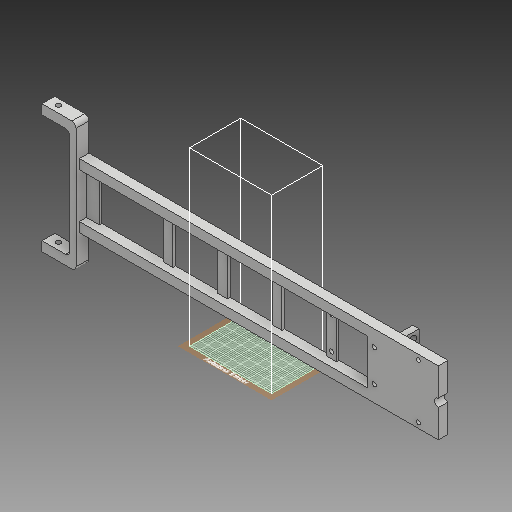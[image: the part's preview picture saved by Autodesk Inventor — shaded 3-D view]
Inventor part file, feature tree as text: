
AUTODESK INVENTOR PART (.ipt)
format: ipt  version: 2018 (Build 220112000, 112)  size: 913,408 bytes
history: native  units: mm
features: sketch x64, extrude x49, fillet x13, hole x6, plane x1
ambient origin geometry x8: Origin, YZ Plane, XZ Plane, XY Plane, X Axis, Y Axis, Z Axis, Center Point
bodies: Solid1 (feature_tree)
feature tree (133):
  extrude  "Extrusion1"  Depth=50.0mm
  hole  "Hole1"  [1 undecoded]
  hole  "Hole2"  [1 undecoded]
  extrude  "Extrusion2"  Depth=25.0mm
  extrude  "Extrusion3"  Depth=25.0mm
  extrude  "Extrusion4"  Depth=5.0mm
  sketch  "Sketch7"  dims[d25=10.0mm d26=5.0mm]
  extrude  "Extrusion5"  Depth=5.0mm
  extrude  "Extrusion6"  Depth=35.0mm
  extrude  "Extrusion7"  Depth=35.0mm
  extrude  "Extrusion8"  Depth=35.0mm
  extrude  "Extrusion9"  Depth=2.0mm TaperAngle=0.0deg
  extrude  "Extrusion10"  Depth=7.5mm TaperAngle=0.0deg
  extrude  "Extrusion11"  Depth=10.0mm
  extrude  "Extrusion12"  Depth=7.5mm
  fillet  "Fillet1"  Radius=7.5mm
  fillet  "Fillet2"  Radius=25.0mm
  fillet  "Fillet3"  Radius=3.0mm
  fillet  "Fillet4"  Radius=3.2mm
  fillet  "Fillet5"  Radius=2.1mm
  fillet  "Fillet6"  Radius=5.5mm
  extrude  "Extrusion13"  Depth=92.5mm TaperAngle=0.0deg
  sketch  "Sketch17"  dims[d58=4.25mm d59=241.0mm d60=0.0mm]
  hole  "Hole3"  [1 undecoded]
  hole  "Hole4"  [1 undecoded]
  extrude  "Extrusion14"  Depth=5.0mm
  extrude  "Extrusion15"  Depth=2.5mm TaperAngle=0.0deg
  extrude  "Extrusion16"  Depth=6.35mm
  extrude  "Extrusion17"  Depth=2.5mm
  extrude  "Extrusion18"  Depth=14.55mm TaperAngle=0.0deg
  extrude  "Extrusion19"  Depth=0.1mm
  extrude  "Extrusion20"  Depth=3.25mm
  extrude  "Extrusion21"  Depth=3.25mm
  hole  "Hole5"  [1 undecoded]
  extrude  "Extrusion22"  Depth=2.0mm
  extrude  "Extrusion23"  Depth=15.0mm
  extrude  "Extrusion24"  Depth=10.0mm TaperAngle=0.0deg
  hole  "Hole6"  [1 undecoded]
  extrude  "Extrusion25"  Depth=100.0mm TaperAngle=0.0deg
  extrude  "Extrusion26"  Depth=2.0mm TaperAngle=0.0deg
  sketch  "Sketch35"  dims[d116=3.3mm d117=3.3mm]
  plane  "Work Plane1"
  sketch  "Sketch36"  dims[d118=3.3mm d119=3.3mm d120=2.0mm d121=0.0mm]
  extrude  "Extrusion27"  Depth=3.3mm
  extrude  "Extrusion28"  Depth=2.0mm
  fillet  "Fillet7"  Radius=2.0mm
  extrude  "Extrusion29"  Depth=8.0mm
  extrude  "Extrusion30"  Depth=21.0mm
  extrude  "Extrusion31"  Depth=8.5mm
  extrude  "Extrusion32"  Depth=3.5mm
  sketch  "Sketch43"  dims[d142=10.0mm d143=0.0mm d144=7.5mm d145=0.0mm]
  fillet  "Fillet8"  Radius=3.3mm
  extrude  "Extrusion33"  Depth=3.3mm
  extrude  "Extrusion34"  Depth=7.5mm TaperAngle=0.0deg
  extrude  "Extrusion35"  Depth=15.0mm
  extrude  "Extrusion36"  Depth=100.0mm TaperAngle=0.0deg
  extrude  "Extrusion37"  Depth=5.0mm
  fillet  "Fillet9"  Radius=5.0mm
  fillet  "Fillet10"  Radius=37.5mm
  fillet  "Fillet11"  Radius=1.1mm
  fillet  "Fillet12"  Radius=37.5mm
  sketch  "Sketch49"  dims[d170=5.5mm d171=0.0mm d172=10.0mm d173=0.0mm]
  extrude  "Extrusion38"  Depth=3.0mm
  extrude  "Extrusion39"  Depth=10.0mm TaperAngle=0.0deg
  extrude  "Extrusion40"  Depth=74.724mm
  fillet  "Fillet13"  Radius=85.515mm
  extrude  "Extrusion41"  Depth=5.0mm
  extrude  "Extrusion42"  Depth=5.0mm
  sketch  "Sketch55"  dims[d186=10.0mm d187=2.0mm d188=0.0mm]
  extrude  "Extrusion43"  Depth=5.0mm
  extrude  "Extrusion44"  Depth=2.0mm TaperAngle=0.0deg
  sketch  "Sketch58"  dims[d195=1.0mm d196=0.0mm d197=20.0mm]
  extrude  "Extrusion45"  Depth=2.0mm TaperAngle=0.0deg
  extrude  "Extrusion46"  Depth=1.0mm TaperAngle=0.0deg
  sketch  "Sketch61"  dims[d202=2.5mm d203=0.0mm]
  extrude  "Extrusion47"  Depth=10.0mm
  extrude  "Extrusion48"  Depth=20.0mm
  extrude  "Extrusion49"  Depth=7.5mm
  sketch  "Sketch1"  dims[d0=50.0mm d1=50.0mm]
  sketch  "Sketch2"  dims[d2=240.0mm d3=7.5mm]
  sketch  "Sketch3"  dims[d4=7.5mm d5=7.5mm d6=0.0mm]
  sketch  "Sketch4"  dims[d7=6.35mm d8=6.0mm d9=4.0mm d10=2.0mm d11=90.0deg d12=8.0mm d13=20.594885mm d14=25.0mm]
  sketch  "Sketch5"  dims[d15=3.3mm d16=6.0mm d17=4.0mm d18=2.0mm d19=90.0deg d20=8.0mm d21=20.594885mm d22=25.0mm]
  sketch  "Sketch6"  dims[d23=180.0deg d24=5.0mm]
  sketch  "Sketch8"  dims[d27=17.5mm d28=0.0mm d30=35.0mm]
  sketch  "Sketch9"  dims[d31=35.0mm d32=35.0mm]
  sketch  "Sketch10"  dims[d33=35.0mm d34=35.0mm]
  sketch  "Sketch11"  dims[d35=35.0mm d36=2.0mm d37=0.0mm]
  sketch  "Sketch12"  dims[d38=10.0mm d39=7.5mm d40=0.0mm]
  sketch  "Sketch13"  dims[d41=100.0mm d42=10.0mm]
  sketch  "Sketch14"  dims[d43=7.5mm d44=0.0mm d45=7.5mm d46=7.5mm d47=25.0mm d48=0.0mm d49=3.0mm d50=3.2mm d51=2.1mm d52=5.5mm]
  sketch  "Sketch15"  dims[d53=3.3mm d54=92.5mm d55=0.0mm]
  sketch  "Sketch16"  dims[d56=5.5mm d57=3.3mm]
  sketch  "Sketch18"  dims[d61=4.44mm d62=5.0mm]
  sketch  "Sketch19"  dims[d63=2.5mm d64=91.25mm d65=0.0mm]
  sketch  "Sketch20"  dims[d66=30.0mm d67=6.35mm]
  sketch  "Sketch21"  dims[d68=3.8mm d69=0.0mm d70=2.5mm]
  sketch  "Sketch22"  dims[d71=14.55mm d72=0.0mm d73=14.55mm d74=0.0mm]
  sketch  "Sketch23"  dims[d75=0.1mm d76=0.1mm]
  sketch  "Sketch24"  dims[d77=3.25mm d78=3.25mm]
  sketch  "Sketch25"  dims[d79=3.25mm d80=3.25mm]
  sketch  "Sketch26"  dims[d81=35.0mm d82=10.0mm]
  sketch  "Sketch27"  dims[d83=2.0mm d84=0.0mm d85=3.6mm]
  sketch  "Sketch28"  dims[d86=3.6mm]
  sketch  "Sketch29"  dims[d87=3.3mm d88=6.0mm d89=4.0mm d90=2.0mm d91=90.0deg d92=15.0mm d93=20.594885mm]
  sketch  "Sketch30"  dims[d94=3.3mm d95=6.0mm d96=4.0mm d97=2.0mm d98=90.0deg d99=15.0mm d100=20.594885mm d101=6.0mm]
  sketch  "Sketch31"  dims[d102=20.0mm d103=0.0mm d104=10.0mm d105=0.0mm]
  sketch  "Sketch32"  dims[d106=2.0mm d107=0.0mm d108=4.0mm]
  sketch  "Sketch33"  dims[d109=100.0mm d110=0.0mm d111=100.0mm d112=0.0mm]
  sketch  "Sketch34"  dims[d113=5.0mm d114=2.0mm d115=0.0mm]
  sketch  "Sketch37"  dims[d122=5.5mm d123=0.0mm]
  sketch  "Sketch38"  dims[d124=3.3mm d125=6.0mm d126=4.0mm d127=2.0mm d128=90.0deg d129=8.0mm d130=20.594885mm d131=42.0mm]
  sketch  "Sketch39"  dims[d132=17.0mm d133=21.0mm]
  sketch  "Sketch40"  dims[d135=8.5mm d136=15.825mm]
  sketch  "Sketch41"  dims[d137=3.5mm d138=21.0mm d139=3.3mm]
  sketch  "Sketch42"  dims[d140=3.3mm d141=3.3mm]
  sketch  "Sketch44"  dims[d146=100.0mm d147=0.0mm]
  sketch  "Sketch45"  dims[d148=5.0mm d149=6.0mm d150=4.0mm d151=2.0mm d152=90.0deg d153=15.0mm d154=0.0mm d155=3.75mm]
  sketch  "Sketch46"  dims[d156=100.0mm d157=0.0mm d158=100.0mm d159=0.0mm]
  sketch  "Sketch47"  dims[d160=-0.698132mm d161=5.0mm d162=5.0mm d163=37.5mm d164=0.0mm d165=1.1mm d166=37.5mm d167=0.0mm]
  sketch  "Sketch48"  dims[d168=0.2mm d169=3.0mm]
  sketch  "Sketch50"  dims[d174=74.724mm d175=74.724mm d176=85.515mm]
  sketch  "Sketch51"  dims[d177=5.0mm d178=85.515mm]
  sketch  "Sketch52"  dims[d179=5.0mm d180=85.515mm]
  sketch  "Sketch53"  dims[d181=5.0mm d182=85.515mm]
  sketch  "Sketch54"  dims[d183=5.0mm d184=2.0mm d185=0.0mm]
  sketch  "Sketch56"  dims[d189=2.0mm d190=1.0mm d191=0.0mm]
  sketch  "Sketch57"  dims[d192=2.0mm d193=0.0mm d194=10.0mm]
  sketch  "Sketch59"  dims[d198=1.0mm d199=0.0mm d200=7.5mm]
  sketch  "Sketch60"  dims[d201=5.0mm]
  sketch  "Sketch62"  dims[d204=3.25mm]
  sketch  "Sketch63"  dims[d205=3.25mm]
  sketch  "Sketch64"  dims[d206=3.25mm d207=3.25mm d208=6.25mm d209=9.58mm d210=250.0mm d211=0.0mm d212=5.25mm d213=4.3mm d214=0.0mm d215=4.3mm d216=0.0mm d217=0.25mm d218=9.7mm d219=100.0mm d220=0.0mm d221=9.8mm d222=4.5mm d223=4.3mm d224=0.0mm d225=9.8mm d226=4.3mm d227=0.0mm d228=10.0mm d229=0.0mm d230=20.0mm d231=10.0mm d232=0.0mm d233=5.0mm d234=5.0mm d235=10.0mm d236=0.0mm d237=3.65mm d238=7.5mm d239=0.0mm d240=7.5mm d241=0.0mm d242=50.0mm d243=0.0mm]
note: 6 required parameter values undecoded (feature->parameter linkage not recoverable at this tier; creation-order binding heuristic only, values carry confidence <= 0.55)
